# Revit family: equip-sink-elkay-s-lustrrtone-lr1716sc
name_source: partatom
category: Plumbing Fixtures
units: mm (PartAtom-declared; Revit-internal decimal feet)

## family parameters
Always vertical = Yes
Cut with Voids When Loaded = No
OmniClass Number = 23.45.05.14.14.27
OmniClass Title = Service Sinks
Part Type = Normal
Room Calculation Point = No
Round Connector Dimension = Use Radius
Shared = No
Work Plane-Based = Yes

## types (4) — shared parameters
Assembly Code = D2010410
Back Faucet CL to Back = 0' - 2 1/4"
Back Faucet Hole One = No
Back Faucet Hole One Top = 0' - 0 1/8"
Back Faucet Hole One to CL = 0' - 4"
Back Faucet Hole Three = No
Back Faucet Hole Three Top = 0' - 0 1/8"
Back Faucet Hole Two = Yes
Back Faucet Hole Two Top = 0' - 0 1/2"
Bowl Drain Location FB = 0' - 5"
Bowl Length = 1' - 2"
Bowl Width = 0' - 10"
CW Flow Rate = 2 GPM
Default Elevation = 3' - 0"
Description = Lustertone Single Bowl Sink
Drain CL LR to Left Bowl Edge = 0' - 7"
Drain Material = Metal - Steel - Stainless - Chrome
Drain Part = LK18
Faucet Material = Metal - Steel - Stainless - Chrome
Faucet Part = LK500GN04T4
Faucet Plan = Yes
HW Flow Rate = 2 GPM
Manufacturer = Elkay Manufacturing
MasterFormat Number = 22.42.16.16
MasterFormat Title = Commercial Sinks
Minimum Cabinet Width = 24"
Nominal Dia = 0' - 0 3/8"
Nominal Radius = 0' - 0 3/16"
OmniClass Code = 23.45.05.14.14.27
OmniClass Title = Service Sinks
Sanitary Flow Rate = 10 GPM
Sanitary Installation Depth from Top Sink_CounterTop = 1' - 2 1/2"
Sanitary Nominal Dia = 0' - 1 1/2"
Sanitary Nominal Radius = 0' - 0 3/4"
Sink Ledge Back Width = 0' - 4 1/4"
Sink Ledge Back Width Hidden = 0' - 4 1/4"
Sink Ledge Front Width = 0' - 1 3/4"
Sink Ledge Front Width Hidden = 0' - 1 3/4"
Sink Ledge Left Width = 0' - 1 1/2"
Sink Ledge Left Width Hidden = 0' - 1 1/2"
Sink Ledge Right Width = 0' - 1 1/2"
Sink Ledge Right Width Hidden = 0' - 1 1/2"
Sink Length = 1' - 5"
Sink Material = Metal - Steel - Stainless - Chrome
Sink Width = 1' - 4"
Specification Sheet URL = http://www.elkayusa.com
Stem Material = Metal - Steel
Supply Cold CL F/B to Back = 0' - 2"
Supply Cold CL L/R to Bowl CL = 0' - 0 1/64"
Supply Hot CL F/B to Back = 0' - 2 1/2"
Supply Hot CL L/R to Bowl CL = 0' - 0 1/64"
Trap Part = LK500
URL = www.elkayusa.com
Wall Face to Back Face of Bowl = 0' - 6 1/4"
Wall Face to Drain Trap CL = 0' - 9 1/32"

## per-type parameters (varying)
| type | Bowl Depth | Sink Part |
| LR1716SC | 0' - 7 5/8" | LR17161 |
| LRAD171655SC | 0' - 5 1/2" | LRAD1716551 |
| LRAD171660SC | 0' - 6" | LRAD1716601 |
| LRAD171665SC | 0' - 6 1/2" | LRAD1716651 |

note: column(s) folded — value = type name in every type: Model

## geometry (parser evidence)
native form markers: Blend x2, Sweep x12
no freeform markers — native parametric forms only
